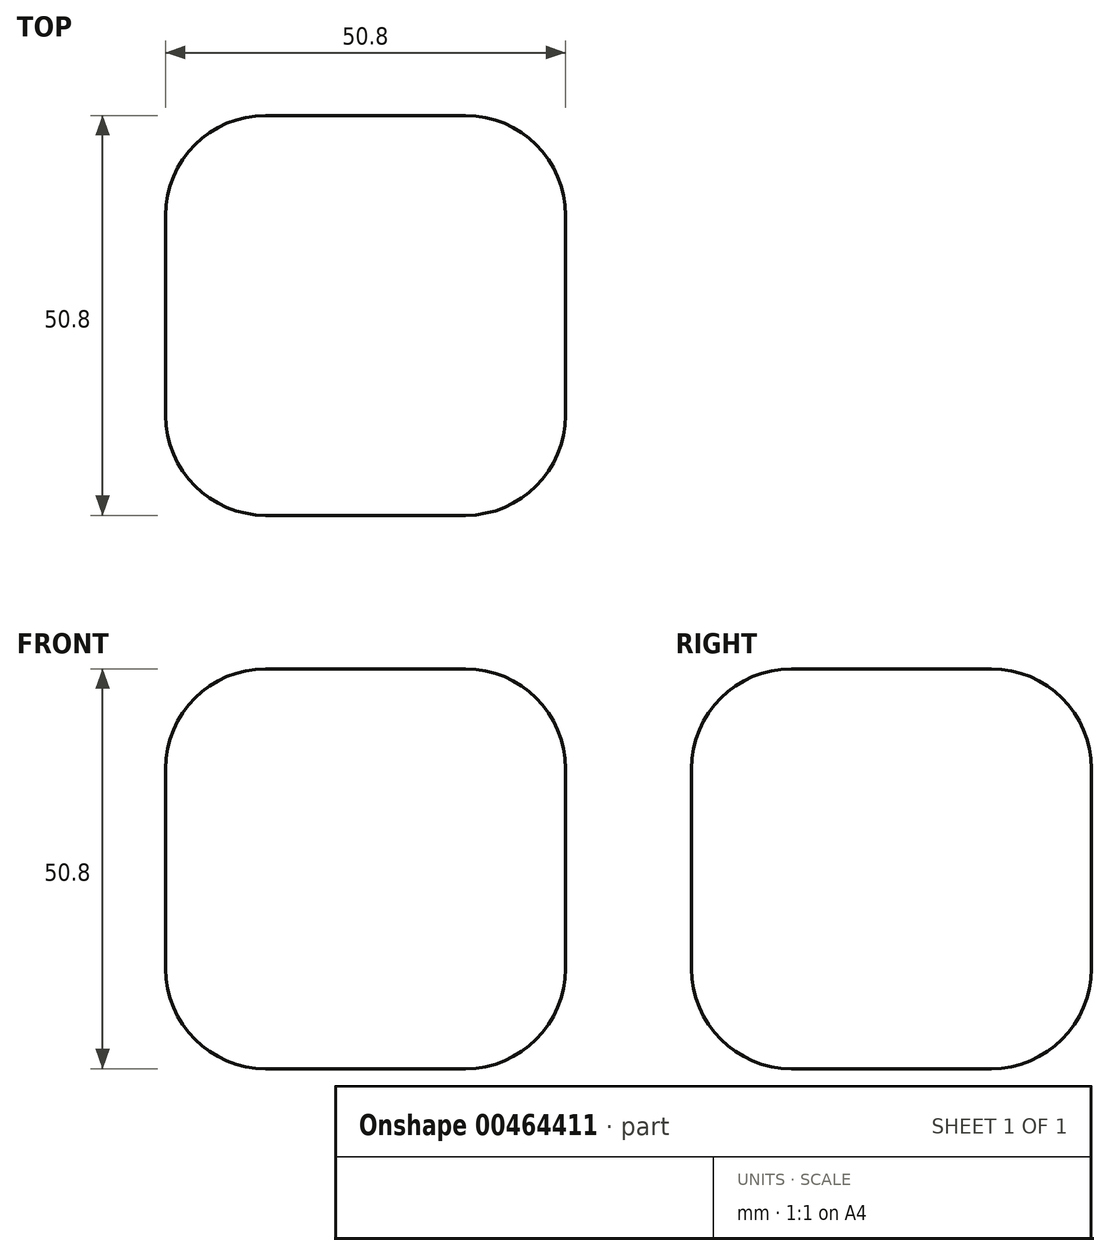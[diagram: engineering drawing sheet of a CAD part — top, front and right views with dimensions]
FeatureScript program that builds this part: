
annotation { "Feature Type Name" : "Feature", "Feature Type Description" : "" }
export const myFeature = defineFeature(function(context is Context, id is Id, definition is map)
    precondition{}
    {
        {
            var Q0;
            Q0=qCreatedBy(makeId("Top.planeOp"),FACE);
            var sketch = newSketch(context, id + "F0", { "sketchPlane" : qUnion([Q0])});
            skLineSegment(sketch, "E0.bottom", {"start": v(-28.93, 21.16) * mm, "end": v(21.87, 21.16) * mm});
            skLineSegment(sketch, "E0.top", {"start": v(-28.93, -29.64) * mm, "end": v(21.87, -29.64) * mm});
            skLineSegment(sketch, "E0.left", {"start": v(-28.93, 21.16) * mm, "end": v(-28.93, -29.64) * mm});
            skLineSegment(sketch, "E0.right", {"start": v(21.87, 21.16) * mm, "end": v(21.87, -29.64) * mm});
            skSolve(sketch);
        }
        {
            var Q0;
            Q0=makeQuery(id+"F0.imprint","IMPRINT",FACE,{"disambiguationData":[TD([[makeQuery(id+"F0.imprint","IMPRINT",EDGE,{"derivedFrom":sQuery(id+"F0.wireOp",EDGE,"E0.bottom")}),-1.0]])]});
            extrude(context, id + "F1", {"entities" : qUnion([Q0]), "depth" : 25.4 * mm});
        }
        {
            var Q0;
            Q0=makeQuery(id+"F1.opExtrude","CAP_FACE",FACE,{"disambiguationData":[OSD([sQuery(id+"F0.wireOp",EDGE,"E0.bottom"),sQuery(id+"F0.wireOp",EDGE,"E0.top"),sQuery(id+"F0.wireOp",EDGE,"E0.left"),sQuery(id+"F0.wireOp",EDGE,"E0.right")])],"isStart":true});
            extrude(context, id + "F2", {"entities" : qUnion([Q0]), "operationType" : NewBodyOperationType.ADD, "depth" : 25.4 * mm});
        }
        {
            var Q0;
            Q0=makeQuery(id+"F1.opExtrude","CAP_EDGE",EDGE,{"disambiguationData":[OSD([sQuery(id+"F0.wireOp",EDGE,"E0.top")])],"isStart":false});
            var Q1;
            Q1=makeQuery(id+"F1.opExtrude","CAP_EDGE",EDGE,{"disambiguationData":[OSD([sQuery(id+"F0.wireOp",EDGE,"E0.left")])],"isStart":false});
            var Q2;
            Q2=makeQuery(id+"F1.opExtrude","CAP_EDGE",EDGE,{"disambiguationData":[OSD([sQuery(id+"F0.wireOp",EDGE,"E0.bottom")])],"isStart":false});
            var Q3;
            Q3=makeQuery(id+"F1.opExtrude","CAP_EDGE",EDGE,{"disambiguationData":[OSD([sQuery(id+"F0.wireOp",EDGE,"E0.right")])],"isStart":false});
            fillet(context, id + "F3", {"entities" : qUnion([Q0, Q1, Q2, Q3]), "radius" : 12.7 * mm, "tangentPropagation" : true, "allowEdgeOverflow" : false});
        }
        {
            var Q0;
            Q0=makeQuery(id+"F2.opExtrude","CAP_EDGE",EDGE,{"disambiguationData":[OSD([sQuery(id+"F0.wireOp",EDGE,"E0.top")])],"isStart":false});
            var Q1;
            Q1=makeQuery(id+"F2.opExtrude","CAP_EDGE",EDGE,{"disambiguationData":[OSD([sQuery(id+"F0.wireOp",EDGE,"E0.left")])],"isStart":false});
            var Q2;
            Q2=makeQuery(id+"F2.opExtrude","CAP_EDGE",EDGE,{"disambiguationData":[OSD([sQuery(id+"F0.wireOp",EDGE,"E0.bottom")])],"isStart":false});
            var Q3;
            Q3=makeQuery(id+"F2.opExtrude","CAP_EDGE",EDGE,{"disambiguationData":[OSD([sQuery(id+"F0.wireOp",EDGE,"E0.right")])],"isStart":false});
            fillet(context, id + "F4", {"entities" : qUnion([Q0, Q1, Q2, Q3]), "radius" : 12.7 * mm, "tangentPropagation" : true, "allowEdgeOverflow" : false});
        }
        {
            var Q0;
            {var subQ0=sQuery(id+"F0.wireOp",EDGE,"E0.left");var subQ1=sQuery(id+"F0.wireOp",EDGE,"E0.top");Q0=makeQuery(id+"F2.boolean.opBoolean","MERGE",EDGE,{"derivedFrom":[makeQuery(id+"F1.opExtrude","SWEPT_EDGE",EDGE,{"disambiguationData":[OSD([subQ1,subQ0])]}),makeQuery(id+"F2.opExtrude","SWEPT_EDGE",EDGE,{"disambiguationData":[OSD([subQ1,subQ0])]})]});}
            var Q1;
            {var subQ0=sQuery(id+"F0.wireOp",EDGE,"E0.left");var subQ1=sQuery(id+"F0.wireOp",EDGE,"E0.bottom");Q1=makeQuery(id+"F2.boolean.opBoolean","MERGE",EDGE,{"derivedFrom":[makeQuery(id+"F1.opExtrude","SWEPT_EDGE",EDGE,{"disambiguationData":[OSD([subQ1,subQ0])]}),makeQuery(id+"F2.opExtrude","SWEPT_EDGE",EDGE,{"disambiguationData":[OSD([subQ1,subQ0])]})]});}
            var Q2;
            {var subQ0=sQuery(id+"F0.wireOp",EDGE,"E0.right");var subQ1=sQuery(id+"F0.wireOp",EDGE,"E0.bottom");Q2=makeQuery(id+"F2.boolean.opBoolean","MERGE",EDGE,{"derivedFrom":[makeQuery(id+"F1.opExtrude","SWEPT_EDGE",EDGE,{"disambiguationData":[OSD([subQ1,subQ0])]}),makeQuery(id+"F2.opExtrude","SWEPT_EDGE",EDGE,{"disambiguationData":[OSD([subQ1,subQ0])]})]});}
            var Q3;
            {var subQ0=sQuery(id+"F0.wireOp",EDGE,"E0.right");var subQ1=sQuery(id+"F0.wireOp",EDGE,"E0.top");Q3=makeQuery(id+"F2.boolean.opBoolean","MERGE",EDGE,{"derivedFrom":[makeQuery(id+"F1.opExtrude","SWEPT_EDGE",EDGE,{"disambiguationData":[OSD([subQ1,subQ0])]}),makeQuery(id+"F2.opExtrude","SWEPT_EDGE",EDGE,{"disambiguationData":[OSD([subQ1,subQ0])]})]});}
            fillet(context, id + "F5", {"entities" : qUnion([Q0, Q1, Q2, Q3]), "radius" : 12.7 * mm, "tangentPropagation" : true, "allowEdgeOverflow" : false});
        }
    });
